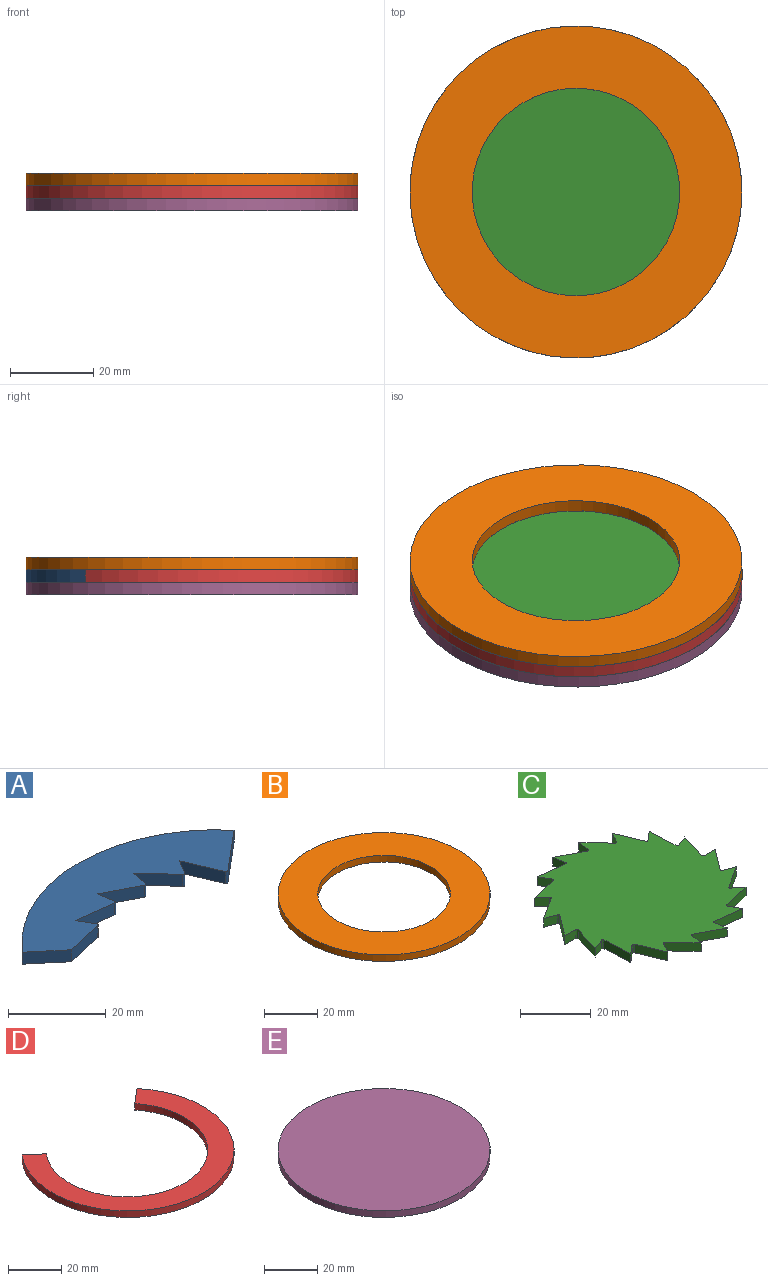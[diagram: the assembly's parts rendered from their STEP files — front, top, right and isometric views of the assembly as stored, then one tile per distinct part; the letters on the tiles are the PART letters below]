
ASSEMBLY  parts=5 mates=4
PART A: 19 faces, bbox 61.3x23.7x3 mm
  f0: plane 7.49x6.92mm, normal (-0.73,-0.68,0), area 30.6mm2, adj f1,f16,f17,f18
  f1: cylinder r=0.4mm len=3mm, axis (0,0,-1), area 2.2mm2, adj f0,f2,f17,f18
  f2: plane 3.86x3mm, normal (0.87,-0.5,0), area 13.4mm2, adj f1,f3,f17,f18
  f3: plane 9.41x3.94mm, normal (-0.92,-0.39,0), area 30.6mm2, adj f2,f4,f17,f18
  f4: cylinder r=0.4mm len=3mm, axis (0,0,-1), area 2.2mm2, adj f3,f5,f17,f18
  f5: plane 11.07x9.29mm, normal (0.64,-0.77,0), area 43.4mm2, adj f4,f6,f17,f18
  f6: cylinder r=40mm len=61.28mm, axis (0,0,-1), area 209.4mm2, adj f5,f7,f17,f18
  f7: plane 7.66x6.43mm, normal (-0.64,-0.77,0), area 30mm2, adj f6,f8,f17,f18
  f8: plane 9.95x3mm, normal (0.22,-0.98,0), area 30.6mm2, adj f7,f9,f17,f18
  f9: cylinder r=0.4mm len=3mm, axis (0,0,-1), area 2.2mm2, adj f8,f10,f17,f18
  f10: plane 3.86x3mm, normal (0.87,0.5,0), area 13.4mm2, adj f9,f11,f17,f18
  f11: plane 10.12x3mm, normal (-0.13,-0.99,0), area 30.6mm2, adj f10,f12,f17,f18
  f12: cylinder r=0.4mm len=3mm, axis (0,0,-1), area 2.2mm2, adj f11,f13,f17,f18
  f13: plane 4.39x3mm, normal (0.98,0.17,0), area 13.4mm2, adj f12,f14,f17,f18
  f14: plane 9.07x4.68mm, normal (-0.46,-0.89,0), area 30.6mm2, adj f13,f15,f17,f18
  f15: cylinder r=0.4mm len=3mm, axis (0,0,-1), area 2.2mm2, adj f14,f16,f17,f18
  f16: plane 4.39x3mm, normal (0.98,-0.17,0), area 13.4mm2, adj f0,f15,f17,f18
  f17: plane 61.28x23.67mm, normal (0,0,1), area 754.6mm2, adj f0,f1,f2,f3,f4,f5,f6,f7
  f18: plane 61.28x23.67mm, normal (0,0,-1), area 754.6mm2, adj f0,f1,f2,f3,f4,f5,f6,f7
PART B: 4 faces, bbox 80x80x3 mm
  f0: cylinder r=25mm len=50mm, axis (0,0,-1), area 471.2mm2, adj f2,f3
  f1: cylinder r=40mm len=80mm, axis (0,0,-1), area 754mm2, adj f2,f3
  f2: plane 80x80mm, normal (0,0,1), area 3063.1mm2, adj f0,f1
  f3: plane 80x80mm, normal (0,0,-1), area 3063.1mm2, adj f0,f1
PART C: 56 faces, bbox 60x59.1x3 mm
  f0: plane 3.86x3mm, normal (-0.87,-0.5,0), area 13.4mm2, adj f1,f53,f54,f55
  f1: cylinder r=0.4mm len=3mm, axis (0,0,-1), area 2.2mm2, adj f0,f2,f54,f55
  f2: plane 9.95x3mm, normal (-0.22,0.98,0), area 30.6mm2, adj f1,f3,f54,f55
  f3: plane 3.41x3mm, normal (-0.64,-0.77,0), area 13.4mm2, adj f2,f4,f54,f55
  f4: cylinder r=0.4mm len=3mm, axis (0,0,-1), area 2.2mm2, adj f3,f5,f54,f55
  f5: plane 8.58x5.52mm, normal (-0.54,0.84,0), area 30.6mm2, adj f4,f6,f54,f55
  f6: plane 4.19x3mm, normal (-0.34,-0.94,0), area 13.4mm2, adj f5,f7,f54,f55
  f7: cylinder r=0.4mm len=3mm, axis (0,0,-1), area 2.2mm2, adj f6,f8,f54,f55
  f8: plane 8.12x6.18mm, normal (-0.8,0.61,0), area 30.6mm2, adj f7,f9,f54,f55
  f9: plane 4.46x3mm, normal (0,-1,0), area 13.4mm2, adj f8,f10,f54,f55
  f10: cylinder r=0.4mm len=3mm, axis (0,0,-1), area 2.2mm2, adj f9,f11,f54,f55
  f11: plane 9.74x3.03mm, normal (-0.95,0.3,0), area 30.6mm2, adj f10,f12,f54,f55
  f12: plane 4.19x3mm, normal (0.34,-0.94,0), area 13.4mm2, adj f11,f13,f54,f55
  f13: cylinder r=0.4mm len=3mm, axis (0,0,-1), area 2.2mm2, adj f12,f14,f54,f55
  f14: plane 10.19x3mm, normal (-1,-0.05,0), area 30.6mm2, adj f13,f15,f54,f55
  f15: plane 3.41x3mm, normal (0.64,-0.77,0), area 13.4mm2, adj f14,f16,f54,f55
  f16: cylinder r=0.4mm len=3mm, axis (0,0,-1), area 2.2mm2, adj f15,f17,f54,f55
  f17: plane 9.41x3.94mm, normal (-0.92,-0.39,0), area 30.6mm2, adj f16,f18,f54,f55
  f18: plane 3.86x3mm, normal (0.87,-0.5,0), area 13.4mm2, adj f17,f19,f54,f55
  f19: cylinder r=0.4mm len=3mm, axis (0,0,-1), area 2.2mm2, adj f18,f20,f54,f55
  f20: plane 7.49x6.92mm, normal (-0.73,-0.68,0), area 30.6mm2, adj f19,f21,f54,f55
  f21: plane 4.39x3mm, normal (0.98,-0.17,0), area 13.4mm2, adj f20,f22,f54,f55
  f22: cylinder r=0.4mm len=3mm, axis (0,0,-1), area 2.2mm2, adj f21,f23,f54,f55
  f23: plane 9.07x4.68mm, normal (-0.46,-0.89,0), area 30.6mm2, adj f22,f24,f54,f55
  f24: plane 4.39x3mm, normal (0.98,0.17,0), area 13.4mm2, adj f23,f25,f54,f55
  f25: cylinder r=0.4mm len=3mm, axis (0,0,-1), area 2.2mm2, adj f24,f26,f54,f55
  f26: plane 10.12x3mm, normal (-0.13,-0.99,0), area 30.6mm2, adj f25,f27,f54,f55
  f27: plane 3.86x3mm, normal (0.87,0.5,0), area 13.4mm2, adj f26,f28,f54,f55
  f28: cylinder r=0.4mm len=3mm, axis (0,0,-1), area 2.2mm2, adj f27,f29,f54,f55
  f29: plane 9.95x3mm, normal (0.22,-0.98,0), area 30.6mm2, adj f28,f30,f54,f55
  f30: plane 3.41x3mm, normal (0.64,0.77,0), area 13.4mm2, adj f29,f31,f54,f55
  f31: cylinder r=0.4mm len=3mm, axis (0,0,-1), area 2.2mm2, adj f30,f32,f54,f55
  f32: plane 8.58x5.52mm, normal (0.54,-0.84,0), area 30.6mm2, adj f31,f33,f54,f55
  f33: plane 4.19x3mm, normal (0.34,0.94,0), area 13.4mm2, adj f32,f34,f54,f55
  f34: cylinder r=0.4mm len=3mm, axis (0,0,-1), area 2.2mm2, adj f33,f35,f54,f55
  f35: plane 8.12x6.18mm, normal (0.8,-0.61,0), area 30.6mm2, adj f34,f36,f54,f55
  f36: plane 4.46x3mm, normal (0,1,0), area 13.4mm2, adj f35,f37,f54,f55
  f37: cylinder r=0.4mm len=3mm, axis (0,0,-1), area 2.2mm2, adj f36,f38,f54,f55
  f38: plane 9.74x3.03mm, normal (0.95,-0.3,0), area 30.6mm2, adj f37,f39,f54,f55
  f39: plane 4.19x3mm, normal (-0.34,0.94,0), area 13.4mm2, adj f38,f40,f54,f55
  f40: cylinder r=0.4mm len=3mm, axis (0,0,-1), area 2.2mm2, adj f39,f41,f54,f55
  f41: plane 10.19x3mm, normal (1,0.05,0), area 30.6mm2, adj f40,f42,f54,f55
  f42: plane 3.41x3mm, normal (-0.64,0.77,0), area 13.4mm2, adj f41,f43,f54,f55
  f43: cylinder r=0.4mm len=3mm, axis (0,0,-1), area 2.2mm2, adj f42,f44,f54,f55
  f44: plane 9.41x3.94mm, normal (0.92,0.39,0), area 30.6mm2, adj f43,f45,f54,f55
  f45: plane 3.86x3mm, normal (-0.87,0.5,0), area 13.4mm2, adj f44,f46,f54,f55
  f46: cylinder r=0.4mm len=3mm, axis (0,0,-1), area 2.2mm2, adj f45,f47,f54,f55
  f47: plane 7.49x6.92mm, normal (0.73,0.68,0), area 30.6mm2, adj f46,f48,f54,f55
  f48: plane 4.39x3mm, normal (-0.98,0.17,0), area 13.4mm2, adj f47,f49,f54,f55
  f49: cylinder r=0.4mm len=3mm, axis (0,0,-1), area 2.2mm2, adj f48,f50,f54,f55
  f50: plane 9.07x4.68mm, normal (0.46,0.89,0), area 30.6mm2, adj f49,f51,f54,f55
  f51: plane 4.39x3mm, normal (-0.98,-0.17,0), area 13.4mm2, adj f50,f52,f54,f55
  f52: cylinder r=0.4mm len=3mm, axis (0,0,-1), area 2.2mm2, adj f51,f53,f54,f55
  f53: plane 10.12x3mm, normal (0.13,0.99,0), area 30.6mm2, adj f0,f52,f54,f55
  f54: plane 60x59.09mm, normal (0,0,1), area 2309.9mm2, adj f0,f1,f2,f3,f4,f5,f6,f7
  f55: plane 60x59.09mm, normal (0,0,-1), area 2309.9mm2, adj f0,f1,f2,f3,f4,f5,f6,f7
PART D: 6 faces, bbox 80x65.7x3 mm
  f0: plane 7.01x5.88mm, normal (0.64,0.77,0), area 27.5mm2, adj f1,f3,f4,f5
  f1: cylinder r=40mm len=80mm, axis (0,0,-1), area 544.5mm2, adj f0,f2,f4,f5
  f2: plane 7.55x6.33mm, normal (-0.64,0.77,0), area 29.6mm2, adj f1,f3,f4,f5
  f3: cylinder r=30.5mm len=61mm, axis (0,0,-1), area 415.2mm2, adj f0,f2,f4,f5
  f4: plane 80x65.71mm, normal (0,0,1), area 1519.5mm2, adj f0,f1,f2,f3
  f5: plane 80x65.71mm, normal (0,0,-1), area 1519.5mm2, adj f0,f1,f2,f3
PART E: 3 faces, bbox 80x80x3 mm
  f0: cylinder r=40mm len=80mm, axis (0,0,-1), area 754mm2, adj f1,f2
  f1: plane 80x80mm, normal (0,0,1), area 5026.5mm2, adj f0
  f2: plane 80x80mm, normal (0,0,-1), area 5026.5mm2, adj f0
PLACE A t=(1.36,-0.18,1.48)mm
PLACE B t=(0.3,-0.19,4.48)mm
PLACE C rot(axis=(0,0,1),58.9deg) t=(0.3,-0.19,1.48)mm
PLACE D t=(-0.16,-0.19,1.48)mm
PLACE E t=(0.3,-0.19,-1.52)mm fixed
MATE fastened B.f1 <-> D.f1  axis (0,0,-1) through (0.3,-0.19,4.48)mm
MATE revolute C.f55 <-> E.f0  axis (0,0,-1) through (0.3,-0.19,1.48)mm
MATE fastened D.f1 <-> E.f0  axis (0,0,-1) through (0.3,-0.19,1.48)mm
MATE fastened A.f6 <-> E.f0  axis (0,0,-1) through (0.3,-0.19,1.48)mm
